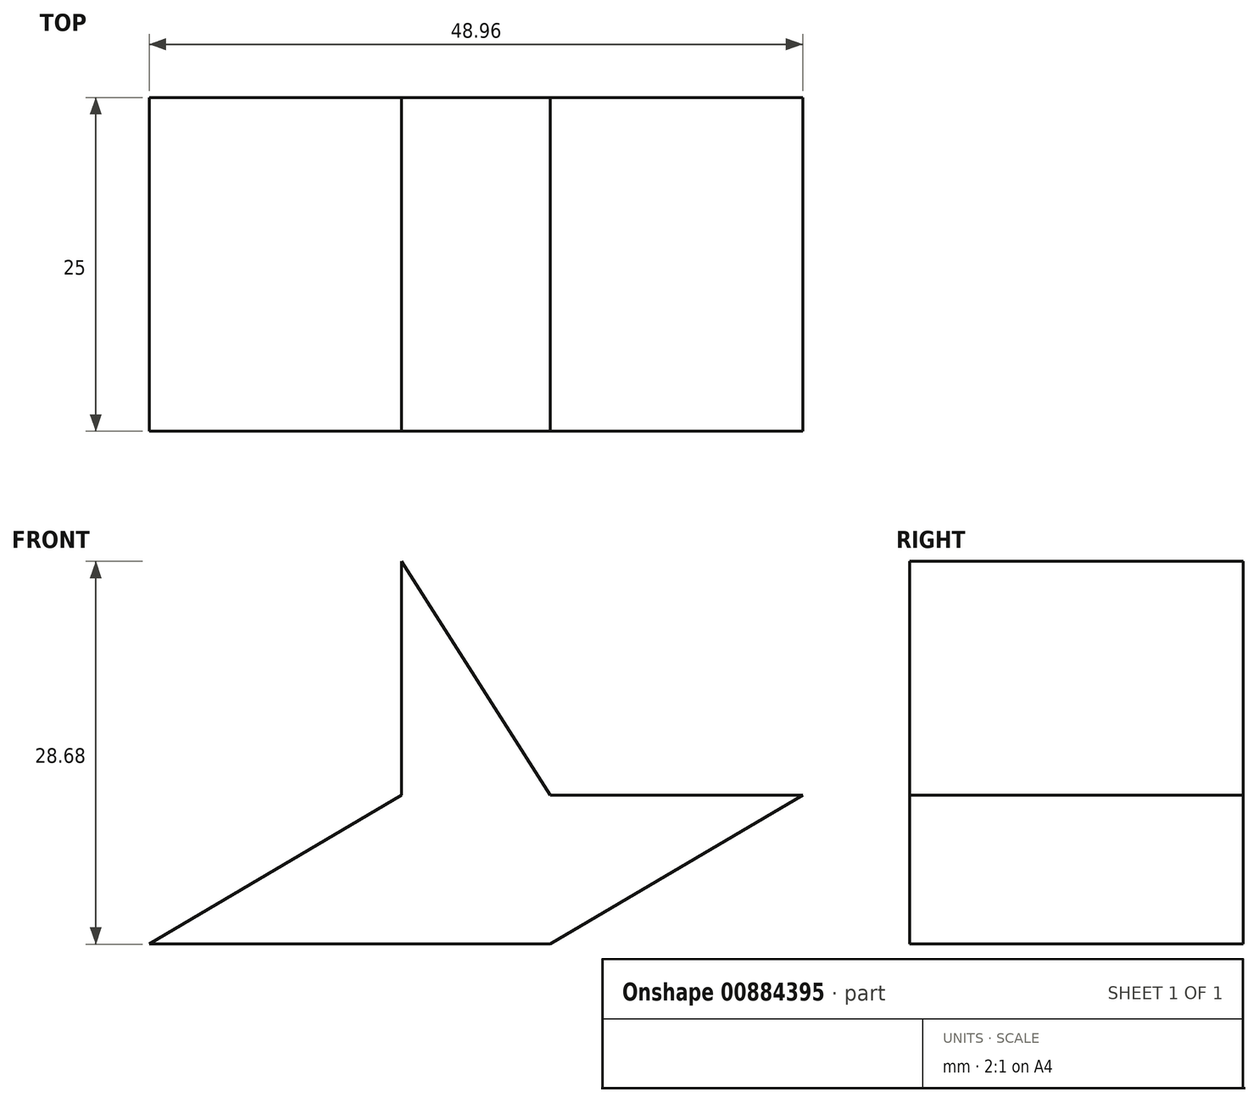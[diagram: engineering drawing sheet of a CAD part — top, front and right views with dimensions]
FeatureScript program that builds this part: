
annotation { "Feature Type Name" : "Feature", "Feature Type Description" : "" }
export const myFeature = defineFeature(function(context is Context, id is Id, definition is map)
    precondition{}
    {
        {
            var Q0;
            Q0=qCreatedBy(makeId("Front.planeOp"),FACE);
            var sketch = newSketch(context, id + "F0", { "sketchPlane" : qUnion([Q0])});
            skLineSegment(sketch, "E0", {"start": v(-84.1, 0) * mm, "end": v(-84.1, 9.46) * mm});
            skLineSegment(sketch, "E1", {"start": v(-84.1, 9.46) * mm, "end": v(-73.59, 9.46) * mm});
            skLineSegment(sketch, "E2", {"start": v(-73.59, 9.46) * mm, "end": v(-73.59, 0) * mm});
            skLineSegment(sketch, "E3", {"start": v(-73.59, 0) * mm, "end": v(-84.1, 0) * mm});
            skLineSegment(sketch, "E4.bottom", {"start": v(33.52, 41.45) * mm, "end": v(22.37, 41.45) * mm});
            skLineSegment(sketch, "E4.top", {"start": v(33.52, 52.6) * mm, "end": v(22.37, 52.6) * mm});
            skLineSegment(sketch, "E4.left", {"start": v(33.52, 41.45) * mm, "end": v(33.52, 52.6) * mm});
            skLineSegment(sketch, "E4.right", {"start": v(22.37, 41.45) * mm, "end": v(22.37, 52.6) * mm});
            skPoint(sketch, "E4.middle", {"position": v(27.94, 47.03) * mm});
            skLineSegment(sketch, "E5", {"start": v(22.37, 41.45) * mm, "end": v(3.46, 41.45) * mm});
            skLineSegment(sketch, "E6", {"start": v(3.46, 41.45) * mm, "end": v(22.37, 52.6) * mm});
            skLineSegment(sketch, "E7", {"start": v(22.37, 41.45) * mm, "end": v(33.52, 41.45) * mm});
            skLineSegment(sketch, "E8", {"start": v(33.52, 41.45) * mm, "end": v(33.52, 23.54) * mm});
            skLineSegment(sketch, "E9", {"start": v(33.52, 23.54) * mm, "end": v(22.37, 41.45) * mm});
            skLineSegment(sketch, "E10", {"start": v(33.52, 52.6) * mm, "end": v(52.42, 52.6) * mm});
            skLineSegment(sketch, "E11", {"start": v(33.52, 41.45) * mm, "end": v(52.42, 52.6) * mm});
            skLineSegment(sketch, "E12", {"start": v(22.37, 52.6) * mm, "end": v(22.37, 70.13) * mm});
            skLineSegment(sketch, "E13", {"start": v(22.37, 70.13) * mm, "end": v(33.52, 52.6) * mm});
            skCircle(sketch, "E14", {"center": v(-111.45, 67.44) * mm, "radius": 10.9 * mm});
            skCircle(sketch, "E15", {"center": v(-111.45, 67.44) * mm, "radius": 14 * mm});
            skCircle(sketch, "E16", {"center": v(-111.45, 67.44) * mm, "radius": 35 * mm});
            skLineSegment(sketch, "E17", {"start": v(-111.45, 67.44) * mm, "end": v(-111.45, 102.44) * mm});
            skLineSegment(sketch, "E18", {"start": v(-111.45, 67.44) * mm, "end": v(-111.45, 32.44) * mm});
            skLineSegment(sketch, "E19", {"start": v(-111.45, 32.44) * mm, "end": v(-111.45, 67.44) * mm});
            skLineSegment(sketch, "E20", {"start": v(-111.45, 67.44) * mm, "end": v(-146.45, 67.44) * mm});
            skLineSegment(sketch, "E21", {"start": v(-111.45, 67.44) * mm, "end": v(-76.45, 67.44) * mm});
            skEllipse(sketch, "E22", {"center": v(-131.37, 67.44) * mm, "majorRadius": 14.56 * mm, "minorRadius": 6.08 * mm, "majorAxis": v(0, 1)});
            skEllipse(sketch, "E23.MirrorC", {"center": v(-91.52, 67.44) * mm, "majorRadius": 14.56 * mm, "minorRadius": 6.08 * mm, "majorAxis": v(0, 1)});
            skEllipse(sketch, "E24", {"center": v(-111.45, 87.48) * mm, "majorRadius": 14.56 * mm, "minorRadius": 6.08 * mm, "majorAxis": v(-1, 0)});
            skEllipse(sketch, "E25.MirrorC", {"center": v(-111.45, 47.4) * mm, "majorRadius": 14.56 * mm, "minorRadius": 6.08 * mm, "majorAxis": v(-1, 0)});
            skEllipse(sketch, "E26.MirrorC", {"center": v(-91.52, 67.44) * mm, "majorRadius": 14.56 * mm, "minorRadius": 6.08 * mm, "majorAxis": v(0, -1)});
            skEllipse(sketch, "E27.MirrorC", {"center": v(-111.45, 87.48) * mm, "majorRadius": 14.56 * mm, "minorRadius": 6.08 * mm, "majorAxis": v(-1, 0)});
            skSolve(sketch);
        }
        {
            var Q0;
            Q0=makeQuery(id+"F0.imprint","IMPRINT",FACE,{"disambiguationData":[TD([[makeQuery(id+"F0.imprint","IMPRINT",EDGE,{"derivedFrom":sQuery(id+"F0.wireOp",EDGE,"E4.right")}),1.0]])]});
            var Q1;
            Q1=makeQuery(id+"F0.imprint","IMPRINT",FACE,{"disambiguationData":[TD([[makeQuery(id+"F0.imprint","IMPRINT",EDGE,{"derivedFrom":sQuery(id+"F0.wireOp",EDGE,"E4.top")}),1.0]])]});
            var Q2;
            Q2=makeQuery(id+"F0.imprint","IMPRINT",FACE,{"disambiguationData":[TD([[makeQuery(id+"F0.imprint","IMPRINT",EDGE,{"derivedFrom":sQuery(id+"F0.wireOp",EDGE,"E7")}),-1.0]])]});
            var Q3;
            Q3=makeQuery(id+"F0.imprint","IMPRINT",FACE,{"disambiguationData":[TD([[makeQuery(id+"F0.imprint","IMPRINT",EDGE,{"derivedFrom":sQuery(id+"F0.wireOp",EDGE,"E4.left")}),-1.0]])]});
            var Q4;
            Q4=makeQuery(id+"F0.imprint","IMPRINT",FACE,{"disambiguationData":[TD([[makeQuery(id+"F0.imprint","IMPRINT",EDGE,{"derivedFrom":sQuery(id+"F0.wireOp",EDGE,"E4.top")}),-1.0]])]});
            extrude(context, id + "F1", {"entities" : qUnion([Q0, Q1, Q2, Q3, Q4]), "depth" : 25 * mm, "offsetDistance" : 25 * mm});
        }
    });
